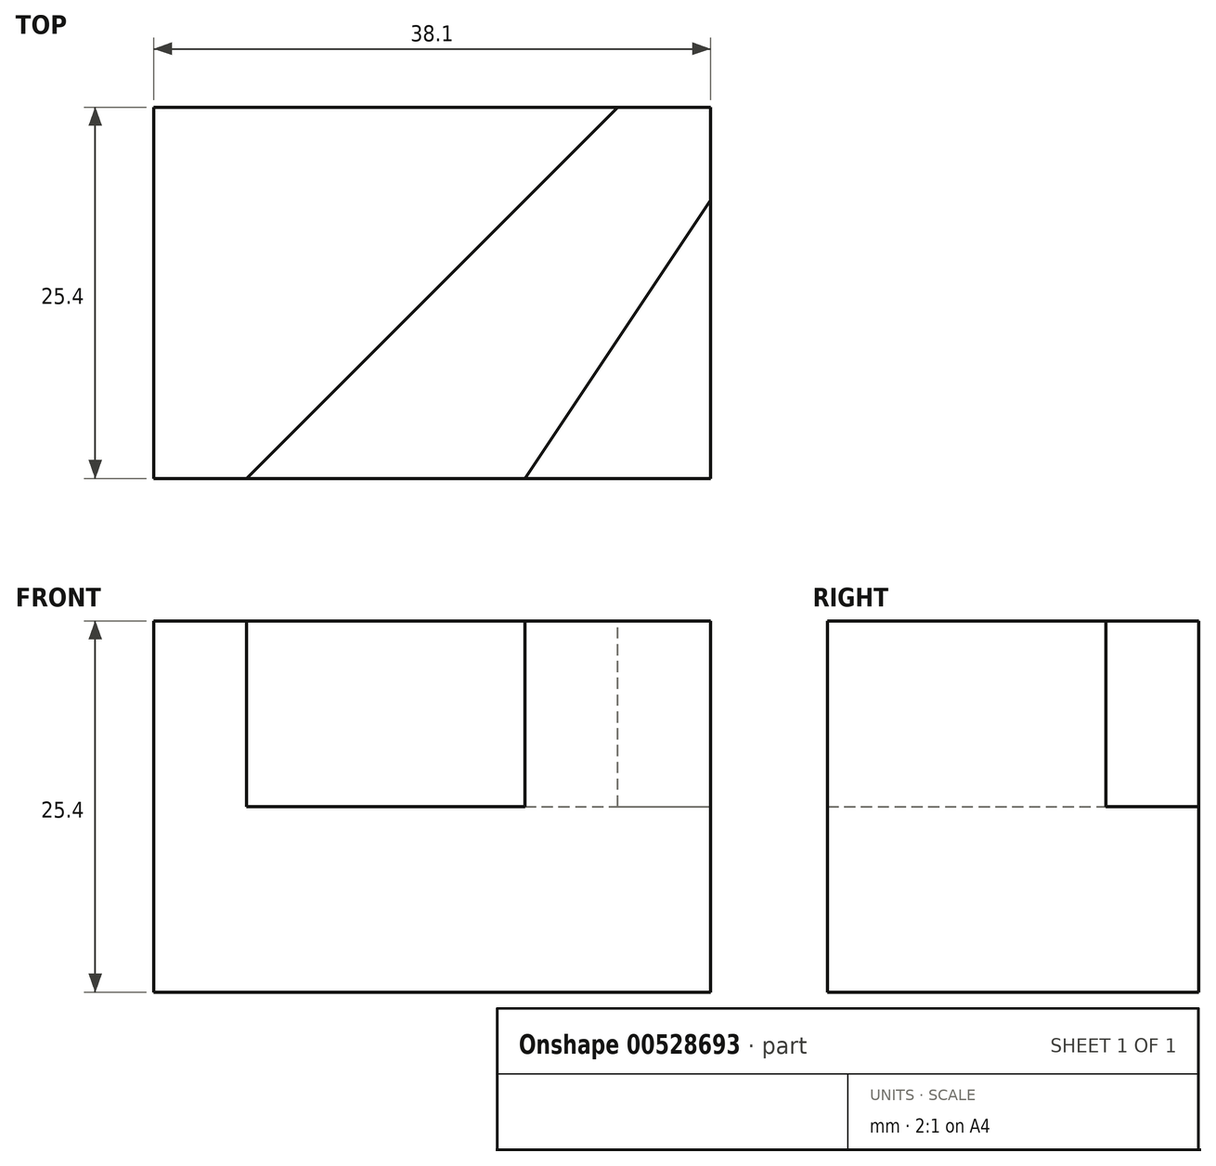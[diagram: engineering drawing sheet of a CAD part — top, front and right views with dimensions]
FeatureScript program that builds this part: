
annotation { "Feature Type Name" : "Feature", "Feature Type Description" : "" }
export const myFeature = defineFeature(function(context is Context, id is Id, definition is map)
    precondition{}
    {
        {
            var Q0;
            Q0=qCreatedBy(makeId("Top.planeOp"),FACE);
            var sketch = newSketch(context, id + "F0", { "sketchPlane" : qUnion([Q0])});
            skLineSegment(sketch, "E0", {"start": v(0, 0) * mm, "end": v(0, 25.4) * mm});
            skLineSegment(sketch, "E1", {"start": v(0, 25.4) * mm, "end": v(38.1, 25.4) * mm});
            skLineSegment(sketch, "E2", {"start": v(0, 0) * mm, "end": v(38.1, 0) * mm});
            skLineSegment(sketch, "E3", {"start": v(38.1, 0) * mm, "end": v(38.1, 25.4) * mm});
            skSolve(sketch);
        }
        {
            var Q0;
            Q0=makeQuery(id+"F0.imprint","IMPRINT",FACE,{"disambiguationData":[TD([[makeQuery(id+"F0.imprint","IMPRINT",EDGE,{"derivedFrom":sQuery(id+"F0.wireOp",EDGE,"E0")}),-1.0]])]});
            extrude(context, id + "F1", {"entities" : qUnion([Q0]), "depth" : 25.4 * mm, "offsetDistance" : 25.4 * mm});
        }
        {
            var Q0;
            Q0=makeQuery(id+"F1.opExtrude","CAP_FACE",FACE,{"disambiguationData":[OSD([sQuery(id+"F0.wireOp",EDGE,"E0"),sQuery(id+"F0.wireOp",EDGE,"E1"),sQuery(id+"F0.wireOp",EDGE,"E2"),sQuery(id+"F0.wireOp",EDGE,"E3")])],"isStart":false});
            var sketch = newSketch(context, id + "F2", { "sketchPlane" : qUnion([Q0])});
            skLineSegment(sketch, "E4", {"start": v(0, 0) * mm, "end": v(6.35, 0) * mm});
            skLineSegment(sketch, "E5", {"start": v(0, 25.4) * mm, "end": v(31.75, 25.4) * mm});
            skLineSegment(sketch, "E6", {"start": v(6.35, 0) * mm, "end": v(31.75, 25.4) * mm});
            skLineSegment(sketch, "E7", {"start": v(38.1, 0) * mm, "end": v(25.4, 0) * mm});
            skLineSegment(sketch, "E8", {"start": v(38.1, 0) * mm, "end": v(38.1, 19.05) * mm});
            skLineSegment(sketch, "E9", {"start": v(25.4, 0) * mm, "end": v(38.1, 19.05) * mm});
            skSolve(sketch);
        }
        {
            var Q0;
            {var subQ0=sQuery(id+"F2.wireOp",EDGE,"E6");Q0=makeQuery(id+"F2.imprint","IMPRINT",FACE,{"disambiguationData":[TD([[makeQuery(id+"F2.imprint","IMPRINT",EDGE,{"derivedFrom":subQ0}),-1.0]])]});}
            extrude(context, id + "F3", {"entities" : qUnion([Q0]), "operationType" : NewBodyOperationType.REMOVE, "oppositeDirection" : true, "depth" : 12.7 * mm, "offsetDistance" : 25.4 * mm});
        }
    });
